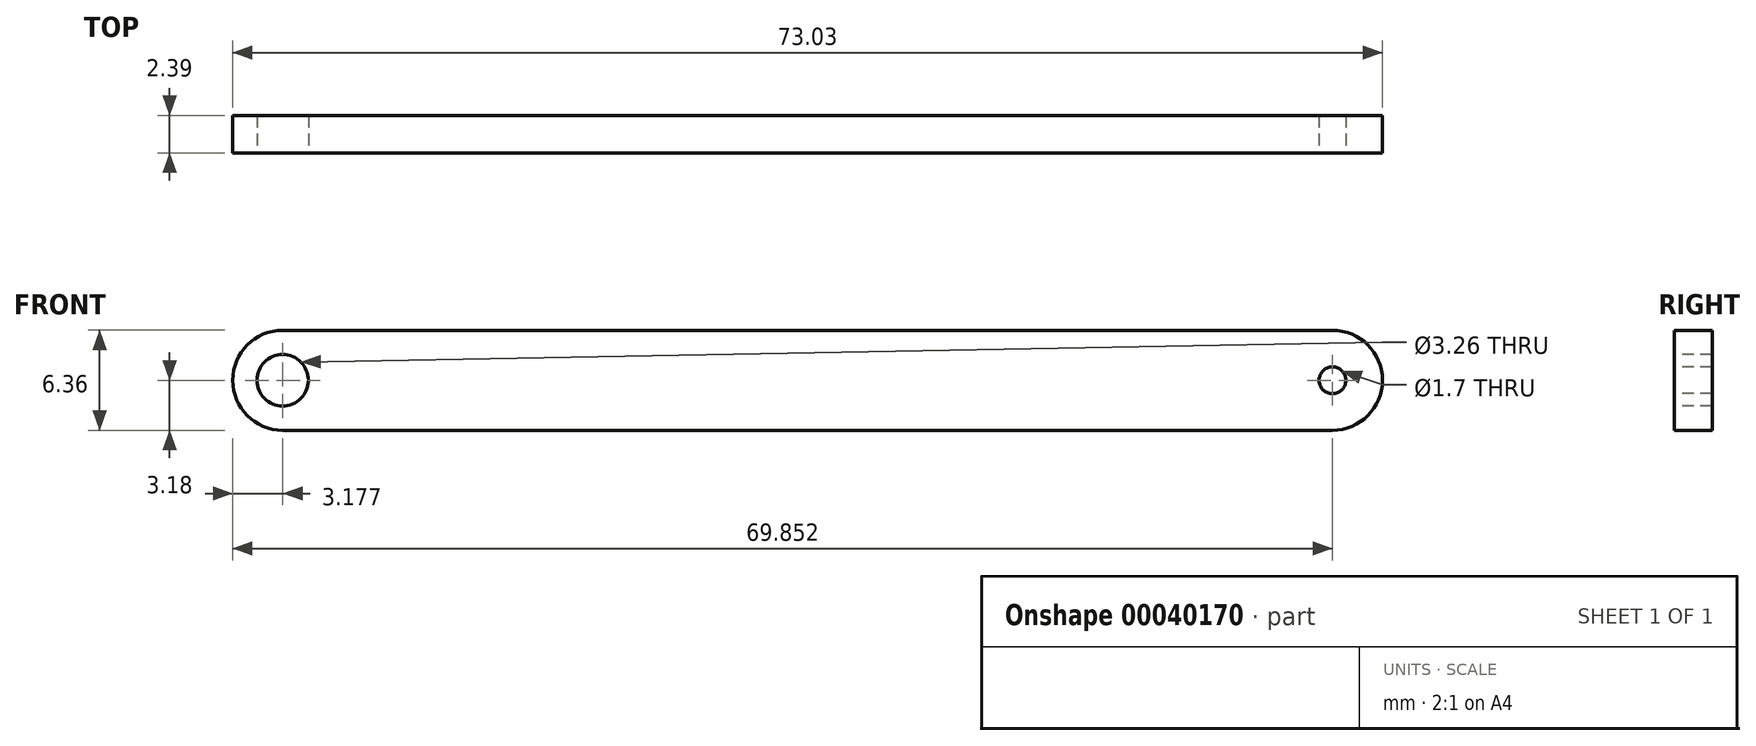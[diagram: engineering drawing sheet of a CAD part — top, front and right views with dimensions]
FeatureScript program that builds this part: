
annotation { "Feature Type Name" : "Feature", "Feature Type Description" : "" }
export const myFeature = defineFeature(function(context is Context, id is Id, definition is map)
    precondition{}
    {
        {
            var Q0;
            Q0=qCreatedBy(makeId("Front.planeOp"),FACE);
            var sketch = newSketch(context, id + "F0", { "sketchPlane" : qUnion([Q0])});
            skLineSegment(sketch, "E0", {"start": v(72.71, 0) * mm, "end": v(72.71, 3.17) * mm, "construction": true});
            skLineSegment(sketch, "E1", {"start": v(72.71, 3.17) * mm, "end": v(6.04, 3.17) * mm});
            skLineSegment(sketch, "E2", {"start": v(6.04, 3.17) * mm, "end": v(6.04, 0) * mm, "construction": true});
            skArc(sketch, "E3", {"start": v(6.04, 3.17) * mm, "mid": v(3.8, 2.25) * mm, "end": v(2.86, 0) * mm});
            skArc(sketch, "E4", {"start": v(72.71, 3.18) * mm, "mid": v(74.96, 2.25) * mm, "end": v(75.89, 0) * mm});
            skLineSegment(sketch, "E5", {"start": v(0, 0) * mm, "end": v(100.12, 0) * mm, "construction": true});
            skArc(sketch, "E6.MirrorCS", {"start": v(6.04, -3.18) * mm, "mid": v(3.8, -2.25) * mm, "end": v(2.86, 0) * mm});
            skLineSegment(sketch, "E7.MirrorCS", {"start": v(72.71, -3.18) * mm, "end": v(6.04, -3.18) * mm});
            skArc(sketch, "E8.MirrorCS", {"start": v(72.71, -3.18) * mm, "mid": v(74.96, -2.25) * mm, "end": v(75.89, 0) * mm});
            skCircle(sketch, "E9", {"center": v(6.04, 0) * mm, "radius": 1.63 * mm});
            skCircle(sketch, "E10", {"center": v(72.71, 0) * mm, "radius": 0.85 * mm});
            skSolve(sketch);
        }
        {
            var Q0;
            Q0 = qSketchRegion(id + "F0", true);
            extrude(context, id + "F1", {"entities" : qUnion([Q0]), "oppositeDirection" : true, "depth" : 2.4 * mm});
        }
    });
